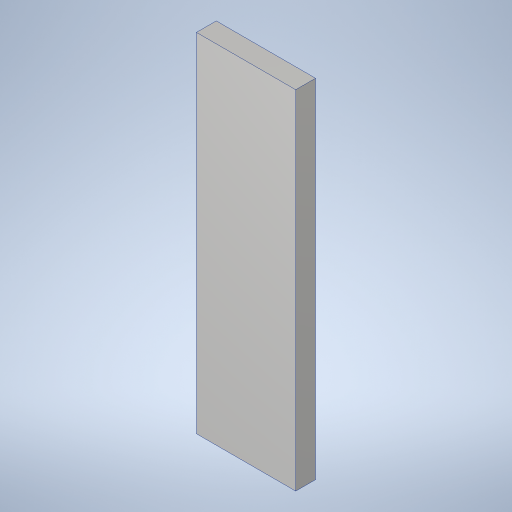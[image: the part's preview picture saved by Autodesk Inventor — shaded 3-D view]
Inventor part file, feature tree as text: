
AUTODESK INVENTOR PART (.ipt)
format: ipt  version: 2023.4 (Build 274418000, 418)  size: 221,696 bytes
history: native  units: in
note: dims shown in document units (in); Inventor stores cm internally (conversion verified against a paired STEP export)
features: extrude x1, sketch x1
ambient origin geometry x8: Origin, YZ Plane, XZ Plane, XY Plane, X Axis, Y Axis, Z Axis, Center Point
bodies: Solid1 (feature_tree)
feature tree (2):
  extrude  "Extrusion1"  Depth=35.0in
  sketch  "Sketch1"  dims[d0=10.0in d1=35.0in d2=2.0in d3=0.0in]
